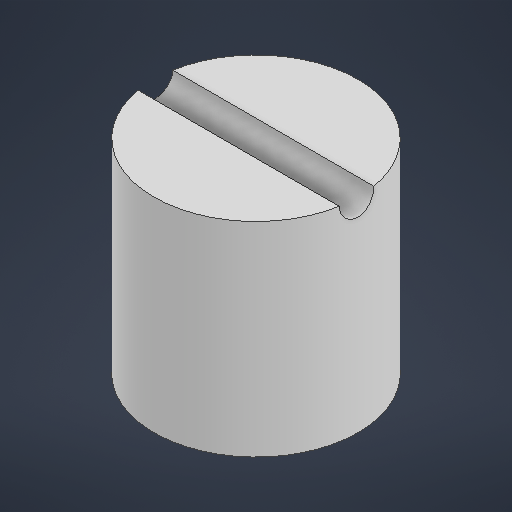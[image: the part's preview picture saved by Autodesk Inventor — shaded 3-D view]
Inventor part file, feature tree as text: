
AUTODESK INVENTOR PART (.ipt)
format: ipt  version: 2025.3 (Build 293356000, 356)  size: 185,856 bytes
history: native  units: mm
features: extrude x3, sketch x2
ambient origin geometry x8: Origin, YZ Plane, XZ Plane, XY Plane, X Axis, Y Axis, Z Axis, Center Point
bodies: Solid1 (feature_tree)
feature tree (5):
  sketch  "Sketch1"  dims[d0=10.0mm d1=8.5mm]
  extrude  "Extrusion1"  Depth=10.0mm
  extrude  "Extrusion2"  Depth=5.0mm TaperAngle=0.0deg
  extrude  "Extrusion4"  Depth=10.0mm
  sketch  "Sketch3"  dims[d2=10.0mm d3=0.0mm d4=5.0mm d5=0.0mm d9=1.7mm d10=5.0mm d11=10.0mm d12=0.0mm]
